# Revit family: Sanitary_Taps-Mixers_DURAVIT-AG_A.1-Single-lever-bathtub-mixer-for-exposed-installation-Chrome-High-Gloss-A152300001_
name_source: partatom
category: Plumbing Fixtures
units: mm (PartAtom-declared; Revit-internal decimal feet)

## family parameters
Cut with Voids When Loaded = Yes
Host = Face
Maintain Annotation Orientation = No
OmniClass Number = 23.31.11.00
OmniClass Title = Faucets
Part Type = Normal
Room Calculation Point = No
Round Connector Dimension = Use Diameter
Shared = No

## types (1)
- A.1 Single lever bathtub mixer for exposed installation Chrome High Gloss - A15230001010
    Default Elevation = 1219 mm
    Depth = 166 mm  [stored 0.544619 ft]
    Description = Duravit A.1 Single lever bathtub mixer for exposed installation, Chrome, Connection type for water supply connection: S-connections, Dimension of connection hose: 1/2", Centre distance: 150 mm ± 20 mm, Ceramic cartridge, recommended operating pressure: 1 - 5 bar, Spray mode: Normal spray, Diverter valve, Non-return valve in the hose connection, Diverter automatically reverts from hand shower to bath spout when turned off, Flow rate (3 bar): 15,5 l/min - A15230001010
    Diameter = 13 mm
    Height = 111 mm
    Installation instructions = https://duravit-public-assets.s3.eu-central-1.amazonaws.com
    Manufacturer = Duravit
    Material 1 = Duravit - Metal - 10 - Chrome
    Model = A.1 Single lever bathtub mixer for exposed installation Chrome High Gloss - A152300001
    Product Documentation Link = https://pro.duravit.com
    Product Page URL = https://pro.duravit.com
    Product data url = https://bimobject.com
    URL = http://pro.duravit.com
    Version = 1
    Weight = 1.30 kg
    Width = 210 mm  [stored 0.688976 ft]

note: [stored X ft] marks values corroborated as IEEE doubles in the binary element streams (Revit-internal decimal feet)

## geometry (parser evidence)
native form markers: Sweep x2
no freeform markers — native parametric forms only
